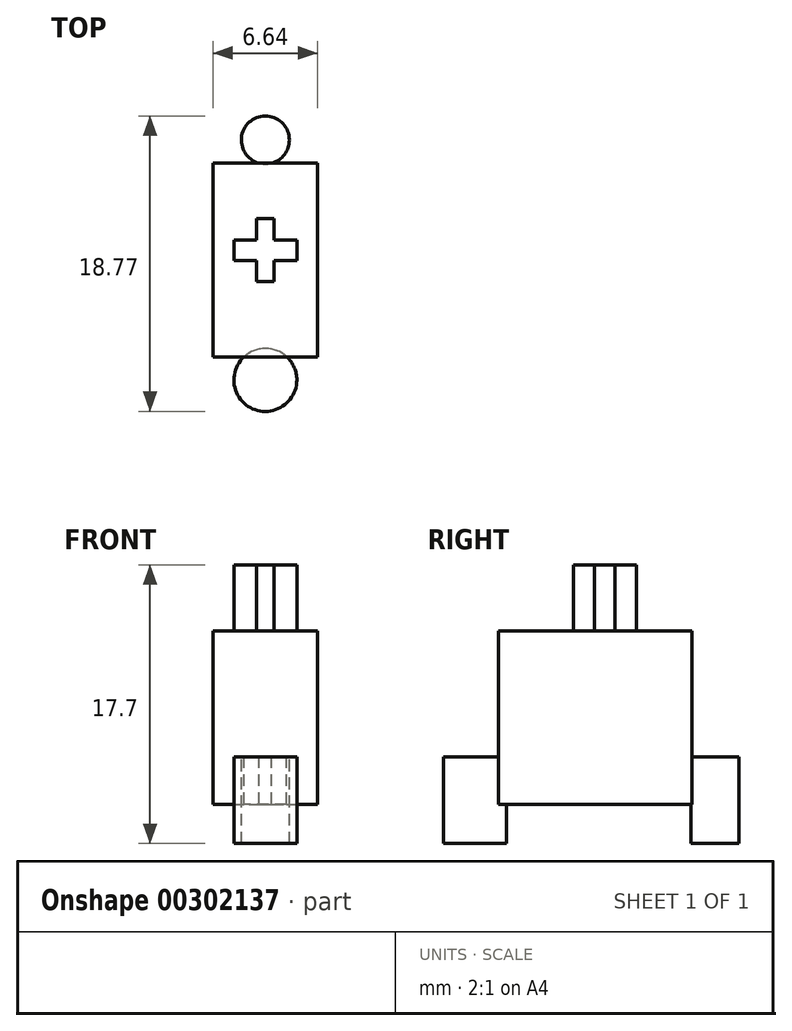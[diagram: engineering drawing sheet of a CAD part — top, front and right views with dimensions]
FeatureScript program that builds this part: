
annotation { "Feature Type Name" : "Feature", "Feature Type Description" : "" }
export const myFeature = defineFeature(function(context is Context, id is Id, definition is map)
    precondition{}
    {
        {
            var Q0;
            Q0=qCreatedBy(makeId("Top.planeOp"),FACE);
            var sketch = newSketch(context, id + "F0", { "sketchPlane" : qUnion([Q0])});
            skLineSegment(sketch, "E0.bottom", {"start": v(-3.33, 5.53) * mm, "end": v(3.32, 5.53) * mm});
            skLineSegment(sketch, "E0.top", {"start": v(-3.32, -6.77) * mm, "end": v(3.33, -6.77) * mm});
            skLineSegment(sketch, "E0.left", {"start": v(-3.32, 5.53) * mm, "end": v(-3.32, -6.77) * mm});
            skLineSegment(sketch, "E0.right", {"start": v(3.33, 5.53) * mm, "end": v(3.33, -6.77) * mm});
            skPoint(sketch, "E1", {"position": v(0, 5.53) * mm});
            skSolve(sketch);
        }
        {
            var Q0;
            Q0=qSketchRegion(id+"F0",true);
            extrude(context, id + "F1", {"entities" : qUnion([Q0]), "depth" : 11 * mm});
        }
        {
            var Q0;
            Q0=qCreatedBy(makeId("Top.planeOp"),FACE);
            var sketch = newSketch(context, id + "F2", { "sketchPlane" : qUnion([Q0])});
            skCircle(sketch, "E2", {"center": v(0, 7) * mm, "radius": 1.52 * mm});
            skCircle(sketch, "E3", {"center": v(0, -8.24) * mm, "radius": 2 * mm});
            skSolve(sketch);
        }
        {
            var Q0;
            Q0=qSketchRegion(id+"F2",true);
            extrude(context, id + "F3", {"entities" : qUnion([Q0]), "operationType" : NewBodyOperationType.ADD, "oppositeDirection" : true, "depth" : 2.5 * mm, "hasSecondDirection" : true, "secondDirectionOppositeDirection" : false, "secondDirectionDepth" : 3 * mm});
        }
        {
            var Q0;
            Q0=qCreatedBy(makeId("Top.planeOp"),FACE);
            cPlane(context, id + "F4", {"entities" : qUnion([Q0]), "cplaneType" : CPlaneType.OFFSET, "offset" : 15.2 * mm, "width" : 150 * mm, "height" : 150 * mm});
        }
        {
            var Q0;
            Q0=makeQuery(id+"F1.opExtrude","CAP_FACE",FACE,{"disambiguationData":[OSD([sQuery(id+"F0.wireOp",EDGE,"E0.bottom"),sQuery(id+"F0.wireOp",EDGE,"E0.top"),sQuery(id+"F0.wireOp",EDGE,"E0.left"),sQuery(id+"F0.wireOp",EDGE,"E0.right")])],"isStart":false});
            var sketch = newSketch(context, id + "F5", { "sketchPlane" : qUnion([Q0])});
            skLineSegment(sketch, "E4.bottom", {"start": v(0.55, 2) * mm, "end": v(-0.55, 2) * mm});
            skLineSegment(sketch, "E4.top", {"start": v(0.55, -2) * mm, "end": v(-0.55, -2) * mm});
            skLineSegment(sketch, "E4.left", {"start": v(0.55, 2) * mm, "end": v(0.55, -2) * mm});
            skLineSegment(sketch, "E4.right", {"start": v(-0.55, 2) * mm, "end": v(-0.55, -2) * mm});
            skPoint(sketch, "E4.middle", {"position": v(0, 0) * mm});
            skLineSegment(sketch, "E5.bottom", {"start": v(2, 0.65) * mm, "end": v(-2, 0.65) * mm});
            skLineSegment(sketch, "E5.top", {"start": v(2, -0.65) * mm, "end": v(-2, -0.65) * mm});
            skLineSegment(sketch, "E5.left", {"start": v(2, 0.65) * mm, "end": v(2, -0.65) * mm});
            skLineSegment(sketch, "E5.right", {"start": v(-2, 0.65) * mm, "end": v(-2, -0.65) * mm});
            skSolve(sketch);
        }
        {
            var Q0;
            Q0=qSketchRegion(id+"F5",true);
            var Q1;
            Q1=qCreatedBy(id+"F4.planeOp",FACE);
            extrude(context, id + "F6", {"entities" : qUnion([Q0]), "operationType" : NewBodyOperationType.ADD, "endBound" : BoundingType.UP_TO_SURFACE, "endBoundEntityFace" : qUnion([Q1]), "depth" : 25 * mm});
        }
    });
